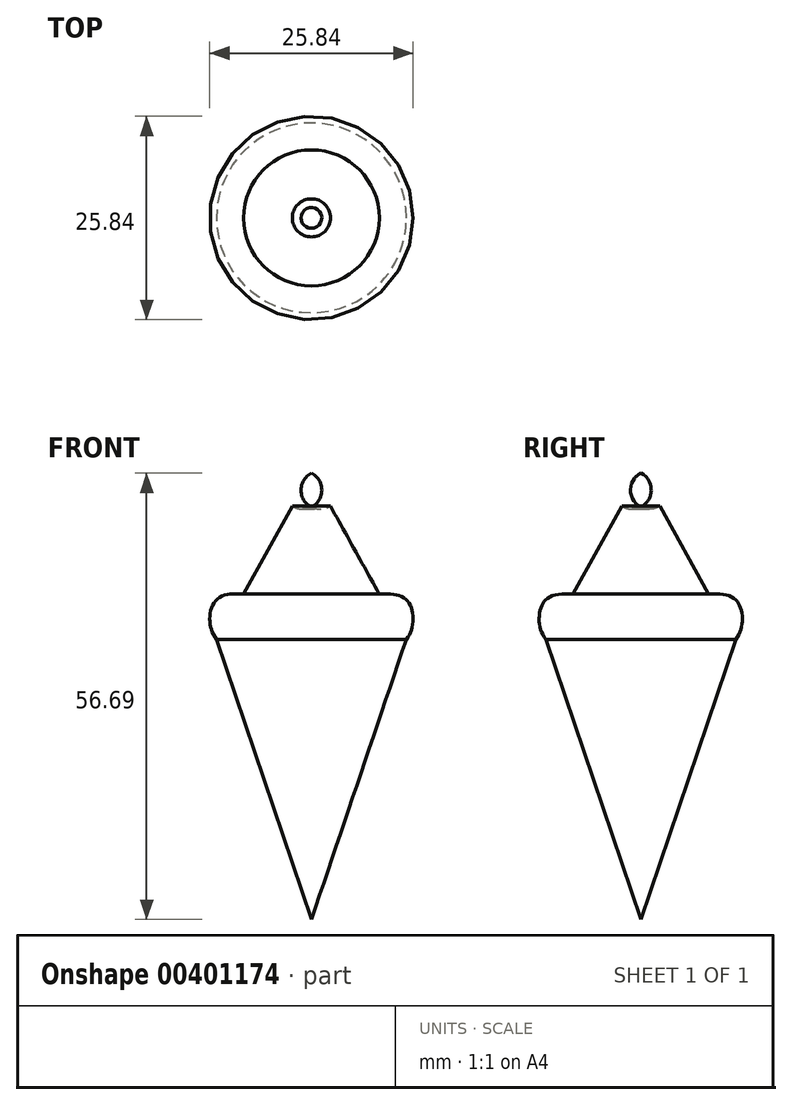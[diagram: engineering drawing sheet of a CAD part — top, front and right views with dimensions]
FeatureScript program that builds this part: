
annotation { "Feature Type Name" : "Feature", "Feature Type Description" : "" }
export const myFeature = defineFeature(function(context is Context, id is Id, definition is map)
    precondition{}
    {
        {
            var Q0;
            Q0=qCreatedBy(makeId("Front.planeOp"),FACE);
            var sketch = newSketch(context, id + "F0", { "sketchPlane" : qUnion([Q0])});
            skLineSegment(sketch, "E0", {"start": v(0, 33) * mm, "end": v(0, -39.54) * mm});
            skLineSegment(sketch, "E1", {"start": v(12.06, 13.95) * mm, "end": v(0, -21.63) * mm});
            skFitSpline(sketch, "E2", {"points": [v(0, 13.26) * mm, v(12.06, 13.95) * mm, v(11.8, 19.18) * mm, v(0, 18.74) * mm], "startDerivative": vector(45.96, -0.85) * mm, "endDerivative": vector(-32.93, 3.48) * mm});
            skLineSegment(sketch, "E3", {"start": v(8.9, 19.18) * mm, "end": v(2.42, 30.86) * mm});
            skArc(sketch, "E4", {"start": v(0, 30.74) * mm, "mid": v(1.23, 30.47) * mm, "end": v(2.42, 30.86) * mm});
            skFitSpline(sketch, "E5", {"points": [v(6.36, -22.3) * mm, v(11.46, -21.63) * mm, v(13.68, -21.63) * mm, v(14.79, -23.2) * mm, v(11.67, -25.16) * mm, v(6.36, -23.05) * mm, v(6.36, -22.3) * mm]});
            skPoint(sketch, "E6.orphan", {"position": v(0, 35.06) * mm});
            skSolve(sketch);
        }
        {
            var Q0;
            {var subQ0=sQuery(id+"F0.wireOp",EDGE,"E2");var subQ1=sQuery(id+"F0.wireOp",EDGE,"E0");var subQ2=makeQuery(id+"F0.imprint","INTERSECT",VERTEX,{"disambiguationData":[OD(0.0)],"derivedFrom":[subQ1,subQ0]});Q0=makeQuery(id+"F0.imprint","IMPRINT",FACE,{"disambiguationData":[TD([[makeQuery(id+"F0.imprint","IMPRINT",EDGE,{"disambiguationData":[TD([[subQ2,1.0]])],"derivedFrom":subQ1}),1.0]])]});}
            var Q1;
            {var subQ1=sQuery(id+"F0.wireOp",EDGE,"E1");var subQ3=sQuery(id+"F0.wireOp",EDGE,"E0");var subQ5=makeQuery(id+"F0.imprint","INTERSECT",VERTEX,{"derivedFrom":[subQ3,subQ1]});Q1=makeQuery(id+"F0.imprint","IMPRINT",FACE,{"disambiguationData":[TD([[makeQuery(id+"F0.imprint","IMPRINT",EDGE,{"disambiguationData":[TD([[subQ5,1.0]])],"derivedFrom":subQ3}),1.0]])]});}
            var Q2;
            {var subQ0=sQuery(id+"F0.wireOp",EDGE,"E2");var subQ1=sQuery(id+"F0.wireOp",EDGE,"E0");var subQ2=makeQuery(id+"F0.imprint","INTERSECT",VERTEX,{"disambiguationData":[OD(1.0)],"derivedFrom":[subQ1,subQ0]});Q2=makeQuery(id+"F0.imprint","IMPRINT",FACE,{"disambiguationData":[TD([[makeQuery(id+"F0.imprint","IMPRINT",EDGE,{"disambiguationData":[TD([[subQ2,1.0]])],"derivedFrom":subQ1}),1.0]])]});}
            var Q3;
            Q3=sQuery(id+"F0.wireOp",EDGE,"E0");
            revolve(context, id + "F1", {"entities" : qUnion([Q0, Q1, Q2]), "axis" : qUnion([Q3]), "revolveType" : RevolveType.FULL});
        }
    });
